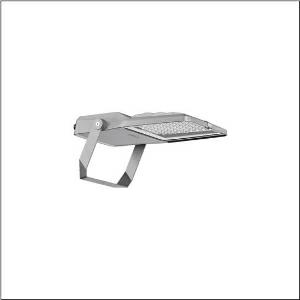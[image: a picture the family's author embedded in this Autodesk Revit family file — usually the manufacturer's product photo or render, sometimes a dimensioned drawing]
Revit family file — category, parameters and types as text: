
# Revit family: floodlight_fl_21_mini___pl61_5xa7776b4c1a_e5f9
name_source: partatom
category: Lighting Fixtures
units: mm (PartAtom-declared; Revit-internal decimal feet)

## family parameters
Cut with Voids When Loaded = No
Host = Face
Light Source = No
Part Type = Normal
Room Calculation Point = No
Round Connector Dimension = Use Diameter
Shared = No

## types (1)
- --- (1 x LED, 6360 lm, 45.7 W, 4000K)
    Apparent Load = 46 VA
    CIE Flux Codes = 33 65 98 100 100
    Color Rendering = 70
    Color Temperature = 4000K
    Default Elevation = 1800 mm
    Description = Floodlight FL 21 mini, floodlight, primary light control with lens, of PMMA, primary optical cover: protective disc, of toughened safety glass, transparent, light distribution: PL61, light emission: direct distribution, installation type: surface-mounted, LED, High Power LED, rated luminous flux: 6.360lm, luminous efficacy: 139lm/W, light colour: 740, colour temperature: 4000K, control gear: D4iSmart Interface (Zhaga), control: overheat protection, constant luminous flux control, time-dependent luminous flux control, flexible luminous flux parameterisation, pre-setting: logarithmic dimming characteristic, with terminal, 6-pole, mains connection: 220..240V, AC, 50/60Hz, start of lifetime: 46W, end of service life: 48W, reduction: 22W, mounting bracket, of diecast aluminium, powder-coated, SITECO metallic grey (DB 702S), corrosivity category C5 mid according to DIN EN ISO 12944, chlorine-resistant, suitable for swimming pools, sealing non-destructively replaceable, mounting bracket, of steel, galvanised, powder-coated, SITECO metallic grey (DB 702S), Smart Interface below and above, protection rating (complete): IP66, insulation class (complete): insulation class II (safety insulation), certification: CE, ENEC, VDE, protection symbol: D, impact resistance: IK08, permissible operating ambient temperature: -40..+40°C, permissible operating ambient temperature for outdoor applications: -40..+50°C, standard: DIN EN 12944, LABS conformity tested according to VDMA 24364:2018-05, packaging unit: 1 piece

Light Distribution: PL61
    Height = 70 mm
    Lamp = 1 x LED
    Lamp Light Flux = 6360 lm
    Lamp Power = 45.7 W
    Lamp count = 1
    Length = 485 mm
    Luminous efficacy = 139 lm/W
    Manufacturer = Siteco
    ModVariant = No
    Model = 5XA7776B4C1A
    Number of Poles = 1
    OnlyDefault = Yes
    Power Factor = 1
    Product Name = Floodlight FL 21 mini | PL61
    Product group = floodlight | pylon annexe
    ProductGroupID = 6201
    Protection Class = Protection class II
    Protection Degree = IP 66
    RLX_Detail_Level = 1
    RLX_Emergency_Light_Flux = 0 lm
    RLX_Emergency_Type = 0
    RLX_Emergency_Type_DB = No
    RlxData = <blob elided: 96161 chars, md5=3011c91b>
    Socket = socket
    Standby Power = 0 W
    System Light Flux = 6360 lm
    System Power = 46 W
    Type Comments = factory setting: luminous flux: 100 % | dim-lin: 254 | 463 mA
    Type Image = l_1006845.jpg
    URL = http://relux.com
    VarID = @adj_102189
    Voltage = 0 V
    Weight = 0.00 kg
    Width = 337 mm

## geometry (parser evidence)
native form markers: Blend x4, Sweep x12
no freeform markers — native parametric forms only
